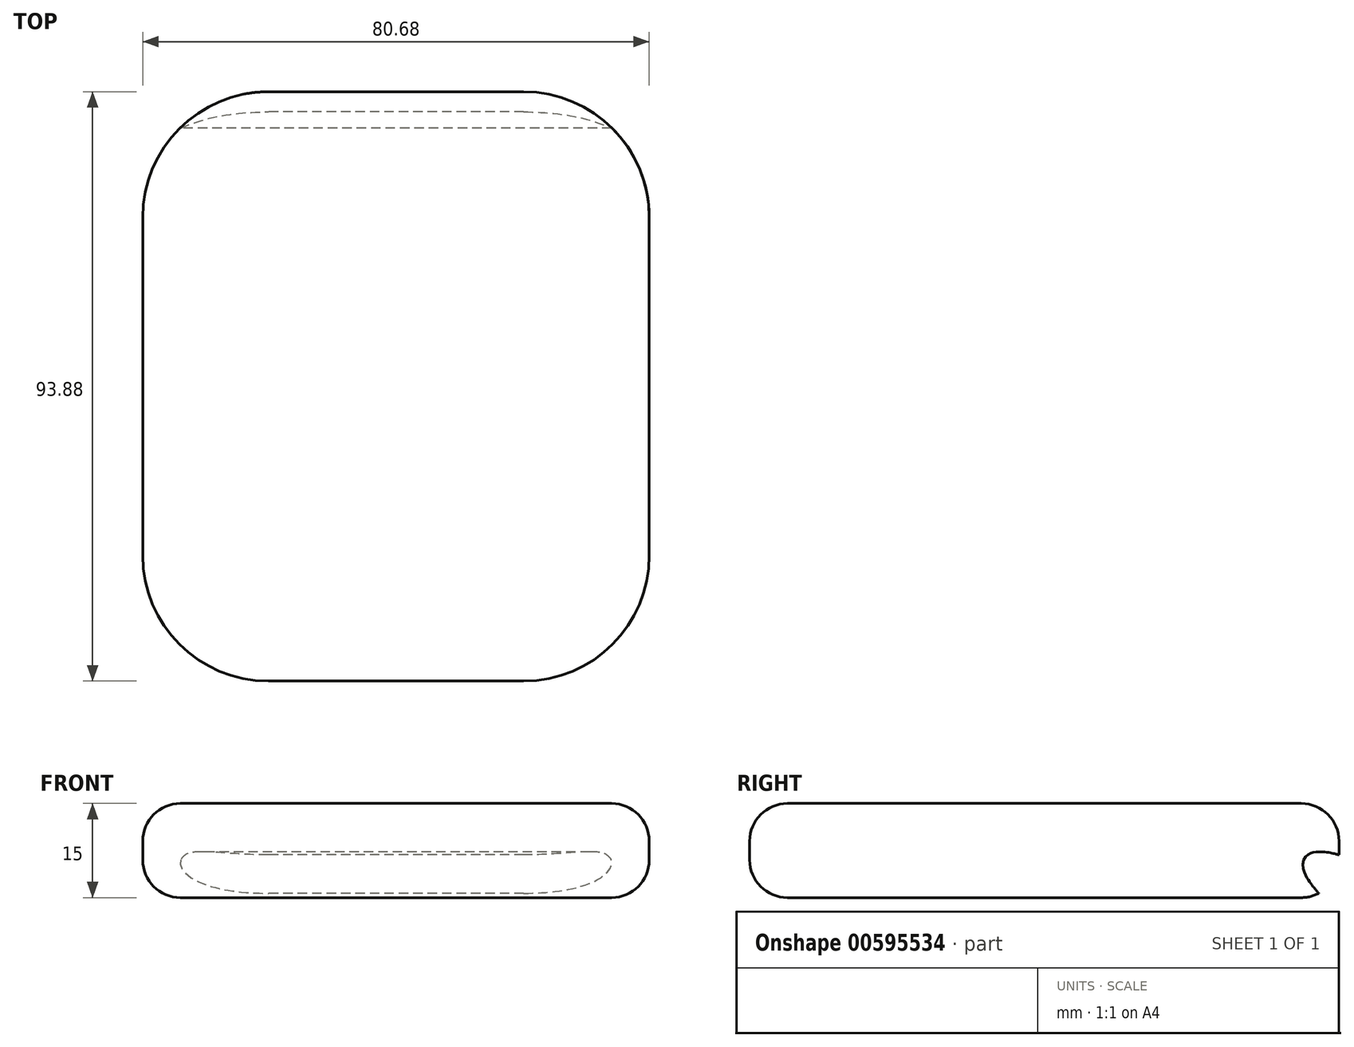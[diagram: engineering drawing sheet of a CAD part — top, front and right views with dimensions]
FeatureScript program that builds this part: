
annotation { "Feature Type Name" : "Feature", "Feature Type Description" : "" }
export const myFeature = defineFeature(function(context is Context, id is Id, definition is map)
    precondition{}
    {
        {
            var Q0;
            Q0=qCreatedBy(makeId("Top.planeOp"),FACE);
            var sketch = newSketch(context, id + "F0", { "sketchPlane" : qUnion([Q0])});
            skLineSegment(sketch, "E0.bottom", {"start": v(40.34, -46.94) * mm, "end": v(-40.34, -46.94) * mm});
            skLineSegment(sketch, "E0.top", {"start": v(40.34, 46.94) * mm, "end": v(-40.34, 46.94) * mm});
            skLineSegment(sketch, "E0.left", {"start": v(40.34, -46.94) * mm, "end": v(40.34, 46.94) * mm});
            skLineSegment(sketch, "E0.right", {"start": v(-40.34, -46.94) * mm, "end": v(-40.34, 46.94) * mm});
            skPoint(sketch, "E0.middle", {"position": v(0, 0) * mm});
            skSolve(sketch);
        }
        {
            var Q0;
            Q0=makeQuery(id+"F0.imprint","IMPRINT",FACE,{"disambiguationData":[TD([[makeQuery(id+"F0.imprint","IMPRINT",EDGE,{"derivedFrom":sQuery(id+"F0.wireOp",EDGE,"E0.bottom")}),-1.0]])]});
            extrude(context, id + "F1", {"entities" : qUnion([Q0]), "endBound" : BoundingType.SYMMETRIC, "depth" : 15 * mm, "offsetDistance" : 25.4 * mm});
        }
        {
            var Q0;
            Q0=makeQuery(id+"F1.opExtrude","SWEPT_EDGE",EDGE,{"disambiguationData":[OSD([sQuery(id+"F0.wireOp",EDGE,"E0.top"),sQuery(id+"F0.wireOp",EDGE,"E0.left")])]});
            var Q1;
            Q1=makeQuery(id+"F1.opExtrude","SWEPT_EDGE",EDGE,{"disambiguationData":[OSD([sQuery(id+"F0.wireOp",EDGE,"E0.top"),sQuery(id+"F0.wireOp",EDGE,"E0.right")])]});
            var Q2;
            Q2=makeQuery(id+"F1.opExtrude","SWEPT_EDGE",EDGE,{"disambiguationData":[OSD([sQuery(id+"F0.wireOp",EDGE,"E0.bottom"),sQuery(id+"F0.wireOp",EDGE,"E0.right")])]});
            var Q3;
            Q3=makeQuery(id+"F1.opExtrude","SWEPT_EDGE",EDGE,{"disambiguationData":[OSD([sQuery(id+"F0.wireOp",EDGE,"E0.bottom"),sQuery(id+"F0.wireOp",EDGE,"E0.left")])]});
            fillet(context, id + "F2", {"entities" : qUnion([Q0, Q1, Q2, Q3]), "radius" : 20 * mm, "tangentPropagation" : true, "allowEdgeOverflow" : false});
        }
        {
            var Q0;
            Q0=makeQuery(id+"F1.opExtrude","CAP_EDGE",EDGE,{"disambiguationData":[OSD([sQuery(id+"F0.wireOp",EDGE,"E0.left")])],"isStart":false});
            var Q1;
            Q1=makeQuery(id+"F1.opExtrude","CAP_EDGE",EDGE,{"disambiguationData":[OSD([sQuery(id+"F0.wireOp",EDGE,"E0.left")])],"isStart":true});
            fillet(context, id + "F3", {"entities" : qUnion([Q0, Q1]), "radius" : 6 * mm, "tangentPropagation" : true, "allowEdgeOverflow" : false});
        }
        {
            var Q0;
            Q0=qCreatedBy(makeId("Right.planeOp"),FACE);
            var sketch = newSketch(context, id + "F4", { "sketchPlane" : qUnion([Q0])});
            skEllipse(sketch, "E1", {"center": v(50.38, -6.88) * mm, "majorRadius": 10.59 * mm, "minorRadius": 4.16 * mm, "majorAxis": v(0.84, -0.54)});
            skSolve(sketch);
        }
        {
            var Q0;
            Q0 = qSketchRegion(id + "F4", true);
            extrude(context, id + "F5", {"entities" : qUnion([Q0]), "operationType" : NewBodyOperationType.REMOVE, "endBound" : BoundingType.SYMMETRIC, "depth" : 90 * mm, "offsetDistance" : 25.4 * mm});
        }
    });
